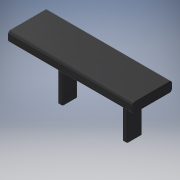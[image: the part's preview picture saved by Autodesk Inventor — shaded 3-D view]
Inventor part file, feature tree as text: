
AUTODESK INVENTOR PART (.ipt)
format: ipt  version: 2018 (Build 220112000, 112)  size: 225,792 bytes
history: native  units: mm
features: extrude x2, fillet x2, sketch x2
ambient origin geometry x8: Origin, YZ Plane, XZ Plane, XY Plane, X Axis, Y Axis, Z Axis, Center Point
bodies: Solid1 (feature_tree)
feature tree (6):
  extrude  "Extrusion1"  Depth=80.0mm
  extrude  "Extrusion2"  Depth=2.0mm
  fillet  "Fillet1"  Radius=30.0mm
  fillet  "Fillet2"  Radius=120.0mm
  sketch  "Sketch1"  dims[d0=250.0mm d1=80.0mm]
  sketch  "Sketch2"  dims[d2=20.0mm d3=0.0mm d4=10.0mm d5=30.0mm d6=120.0mm d7=100.0mm d8=0.0mm d9=5.0mm d10=2.0mm d11=45.0mm]
